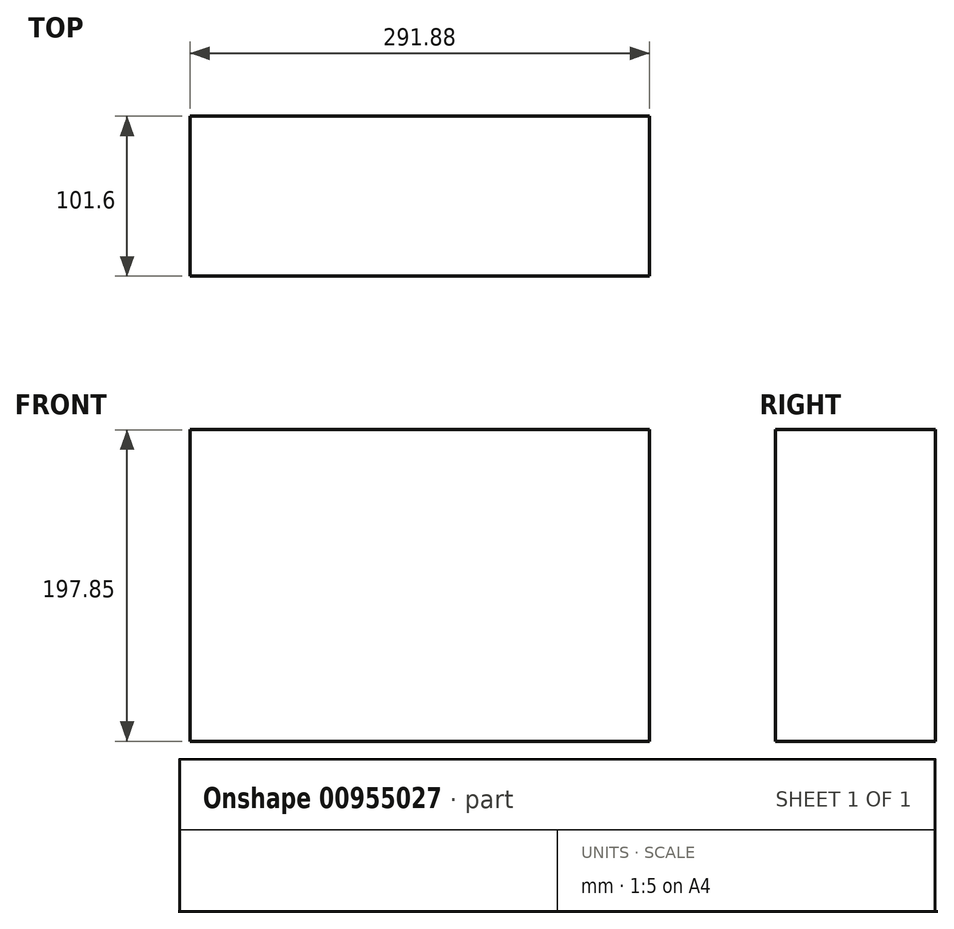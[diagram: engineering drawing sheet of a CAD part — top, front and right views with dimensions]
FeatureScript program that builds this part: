
annotation { "Feature Type Name" : "Feature", "Feature Type Description" : "" }
export const myFeature = defineFeature(function(context is Context, id is Id, definition is map)
    precondition{}
    {
        {
            var Q0;
            Q0=qCreatedBy(makeId("Front.planeOp"),FACE);
            var sketch = newSketch(context, id + "F0", { "sketchPlane" : qUnion([Q0])});
            skLineSegment(sketch, "E0.bottom", {"start": v(-143.81, 98.14) * mm, "end": v(148.07, 98.14) * mm});
            skLineSegment(sketch, "E0.top", {"start": v(-143.81, -99.71) * mm, "end": v(148.07, -99.71) * mm});
            skLineSegment(sketch, "E0.left", {"start": v(-143.81, 98.14) * mm, "end": v(-143.81, -99.71) * mm});
            skLineSegment(sketch, "E0.right", {"start": v(148.07, 98.14) * mm, "end": v(148.07, -99.71) * mm});
            skSolve(sketch);
        }
        {
            var Q0;
            Q0=makeQuery(id+"F0.imprint","IMPRINT",FACE,{"disambiguationData":[TD([[makeQuery(id+"F0.imprint","IMPRINT",EDGE,{"derivedFrom":sQuery(id+"F0.wireOp",EDGE,"E0.bottom")}),-1.0]])]});
            extrude(context, id + "F1", {"entities" : qUnion([Q0]), "depth" : 101.6 * mm, "offsetDistance" : 25.4 * mm, "symmetric" : true});
        }
    });
